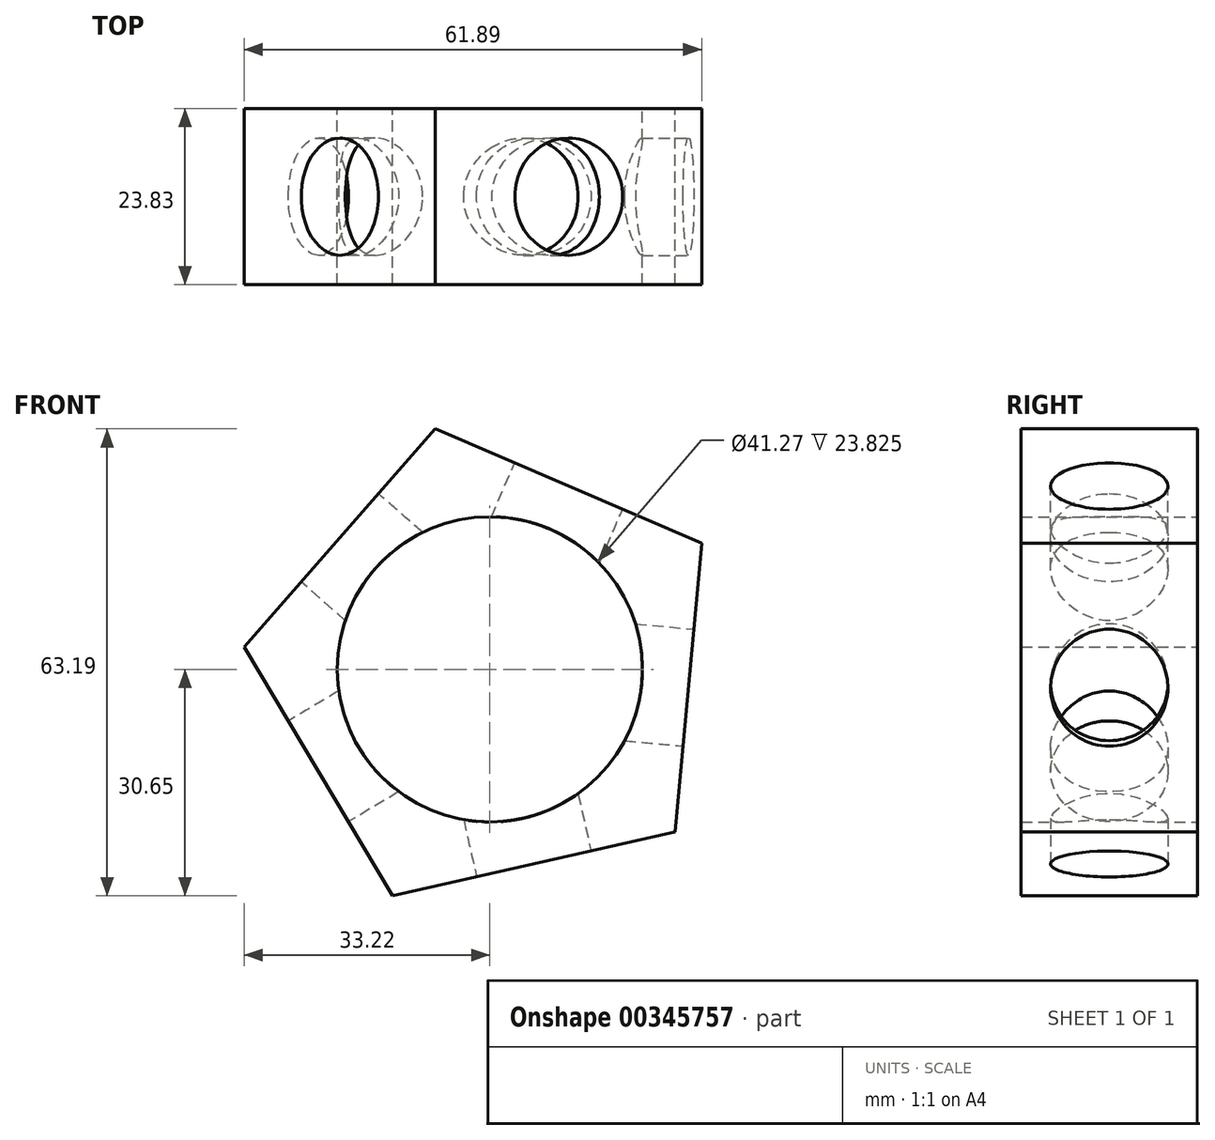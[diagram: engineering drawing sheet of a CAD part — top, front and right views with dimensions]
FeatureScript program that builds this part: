
annotation { "Feature Type Name" : "Feature", "Feature Type Description" : "" }
export const myFeature = defineFeature(function(context is Context, id is Id, definition is map)
    precondition{}
    {
        {
            var Q0;
            Q0=qCreatedBy(makeId("Front.planeOp"),FACE);
            var sketch = newSketch(context, id + "F0", { "sketchPlane" : qUnion([Q0])});
            skCircle(sketch, "E0.cCircle", {"center": v(0, 0) * mm, "radius": 26.99 * mm, "construction": true});
            skLineSegment(sketch, "E0.0", {"start": v(-33.22, 3.06) * mm, "end": v(-7.36, 32.54) * mm});
            skLineSegment(sketch, "E0.1", {"start": v(-7.36, 32.54) * mm, "end": v(28.67, 17.05) * mm});
            skLineSegment(sketch, "E0.2", {"start": v(28.67, 17.05) * mm, "end": v(25.08, -22) * mm});
            skLineSegment(sketch, "E0.3", {"start": v(25.08, -22) * mm, "end": v(-13.17, -30.65) * mm});
            skLineSegment(sketch, "E0.4", {"start": v(-13.17, -30.65) * mm, "end": v(-33.22, 3.06) * mm});
            skPoint(sketch, "E0.0.midPoint", {"position": v(-20.29, 17.8) * mm});
            skCircle(sketch, "E1", {"center": v(0, 0) * mm, "radius": 20.64 * mm});
            skSolve(sketch);
        }
        {
            var Q0;
            Q0=makeQuery(id+"F0.imprint","IMPRINT",FACE,{"disambiguationData":[TD([[makeQuery(id+"F0.imprint","IMPRINT",EDGE,{"derivedFrom":sQuery(id+"F0.wireOp",EDGE,"E0.0")}),-1.0]])]});
            extrude(context, id + "F1", {"entities" : qUnion([Q0]), "depth" : 23.83 * mm});
        }
        {
            var Q0;
            Q0=makeQuery(id+"F1.opExtrude","SWEPT_FACE",FACE,{"disambiguationData":[OSD([sQuery(id+"F0.wireOp",EDGE,"E0.2")])]});
            var sketch = newSketch(context, id + "F2", { "sketchPlane" : qUnion([Q0])});
            skPoint(sketch, "E2", {"position": v(-11.91, 0) * mm});
            skSolve(sketch);
        }
        {
            var Q0;
            Q0=sQuery(id+"F2.wireOp",VERTEX,"E2");
            var Q1;
            Q1=makeQuery(id+"F1.opExtrude","SWEPT_BODY",BODY,{"disambiguationData":[OSD([sQuery(id+"F0.wireOp",EDGE,"E0.0"),sQuery(id+"F0.wireOp",EDGE,"E0.1"),sQuery(id+"F0.wireOp",EDGE,"E0.2"),sQuery(id+"F0.wireOp",EDGE,"E0.3"),sQuery(id+"F0.wireOp",EDGE,"E0.4"),sQuery(id+"F0.wireOp",EDGE,"E1")])]});
            hole(context, id + "F3", {"style" : HoleStyle.SIMPLE, "endStyle" : HoleEndStyle.BLIND, "holeDiameter" : 15.88 * mm, "holeDepth" : 12.7 * mm, "isTappedThrough" : true, "tappedDepth" : 12.7 * mm, "tapClearance" : 3, "locations" : qUnion([Q0]), "scope" : qUnion([Q1])});
        }
        {
            var Q0;
            Q0=makeQuery(id+"F1.opExtrude","SWEPT_FACE",FACE,{"disambiguationData":[OSD([sQuery(id+"F0.wireOp",EDGE,"E0.1")])]});
            var sketch = newSketch(context, id + "F4", { "sketchPlane" : qUnion([Q0])});
            skPoint(sketch, "E3", {"position": v(0, -11.91) * mm});
            skSolve(sketch);
        }
        {
            var Q0;
            Q0=sQuery(id+"F4.wireOp",VERTEX,"E3");
            var Q1;
            Q1=makeQuery(id+"F1.opExtrude","SWEPT_BODY",BODY,{"disambiguationData":[OSD([sQuery(id+"F0.wireOp",EDGE,"E0.0"),sQuery(id+"F0.wireOp",EDGE,"E0.1"),sQuery(id+"F0.wireOp",EDGE,"E0.2"),sQuery(id+"F0.wireOp",EDGE,"E0.3"),sQuery(id+"F0.wireOp",EDGE,"E0.4"),sQuery(id+"F0.wireOp",EDGE,"E1")])]});
            hole(context, id + "F5", {"style" : HoleStyle.SIMPLE, "endStyle" : HoleEndStyle.BLIND, "holeDiameter" : 15.88 * mm, "holeDepth" : 12.7 * mm, "isTappedThrough" : true, "tappedDepth" : 12.7 * mm, "tapClearance" : 3, "locations" : qUnion([Q0]), "scope" : qUnion([Q1])});
        }
        {
            var Q0;
            Q0=makeQuery(id+"F1.opExtrude","SWEPT_FACE",FACE,{"disambiguationData":[OSD([sQuery(id+"F0.wireOp",EDGE,"E0.0")])]});
            var sketch = newSketch(context, id + "F6", { "sketchPlane" : qUnion([Q0])});
            skPoint(sketch, "E4", {"position": v(11.91, 0) * mm});
            skSolve(sketch);
        }
        {
            var Q0;
            Q0=sQuery(id+"F6.wireOp",VERTEX,"E4");
            var Q1;
            Q1=makeQuery(id+"F1.opExtrude","SWEPT_BODY",BODY,{"disambiguationData":[OSD([sQuery(id+"F0.wireOp",EDGE,"E0.0"),sQuery(id+"F0.wireOp",EDGE,"E0.1"),sQuery(id+"F0.wireOp",EDGE,"E0.2"),sQuery(id+"F0.wireOp",EDGE,"E0.3"),sQuery(id+"F0.wireOp",EDGE,"E0.4"),sQuery(id+"F0.wireOp",EDGE,"E1")])]});
            hole(context, id + "F7", {"style" : HoleStyle.SIMPLE, "endStyle" : HoleEndStyle.BLIND, "holeDiameter" : 15.88 * mm, "holeDepth" : 12.7 * mm, "isTappedThrough" : true, "tappedDepth" : 12.7 * mm, "tapClearance" : 3, "locations" : qUnion([Q0]), "scope" : qUnion([Q1])});
        }
        {
            var Q0;
            Q0=makeQuery(id+"F1.opExtrude","SWEPT_FACE",FACE,{"disambiguationData":[OSD([sQuery(id+"F0.wireOp",EDGE,"E0.4")])]});
            var sketch = newSketch(context, id + "F8", { "sketchPlane" : qUnion([Q0])});
            skPoint(sketch, "E5", {"position": v(11.91, 0) * mm});
            skSolve(sketch);
        }
        {
            var Q0;
            Q0=sQuery(id+"F8.wireOp",VERTEX,"E5");
            var Q1;
            Q1=makeQuery(id+"F1.opExtrude","SWEPT_BODY",BODY,{"disambiguationData":[OSD([sQuery(id+"F0.wireOp",EDGE,"E0.0"),sQuery(id+"F0.wireOp",EDGE,"E0.1"),sQuery(id+"F0.wireOp",EDGE,"E0.2"),sQuery(id+"F0.wireOp",EDGE,"E0.3"),sQuery(id+"F0.wireOp",EDGE,"E0.4"),sQuery(id+"F0.wireOp",EDGE,"E1")])]});
            hole(context, id + "F9", {"style" : HoleStyle.SIMPLE, "endStyle" : HoleEndStyle.BLIND, "holeDiameter" : 15.88 * mm, "holeDepth" : 12.7 * mm, "isTappedThrough" : true, "tappedDepth" : 12.7 * mm, "tapClearance" : 3, "locations" : qUnion([Q0]), "scope" : qUnion([Q1])});
        }
        {
            var Q0;
            Q0=makeQuery(id+"F1.opExtrude","SWEPT_FACE",FACE,{"disambiguationData":[OSD([sQuery(id+"F0.wireOp",EDGE,"E0.3")])]});
            var sketch = newSketch(context, id + "F10", { "sketchPlane" : qUnion([Q0])});
            skPoint(sketch, "E6", {"position": v(0, 11.91) * mm});
            skSolve(sketch);
        }
        {
            var Q0;
            Q0=sQuery(id+"F10.wireOp",VERTEX,"E6");
            var Q1;
            Q1=makeQuery(id+"F1.opExtrude","SWEPT_BODY",BODY,{"disambiguationData":[OSD([sQuery(id+"F0.wireOp",EDGE,"E0.0"),sQuery(id+"F0.wireOp",EDGE,"E0.1"),sQuery(id+"F0.wireOp",EDGE,"E0.2"),sQuery(id+"F0.wireOp",EDGE,"E0.3"),sQuery(id+"F0.wireOp",EDGE,"E0.4"),sQuery(id+"F0.wireOp",EDGE,"E1")])]});
            hole(context, id + "F11", {"style" : HoleStyle.SIMPLE, "endStyle" : HoleEndStyle.BLIND, "holeDiameter" : 15.88 * mm, "holeDepth" : 12.7 * mm, "isTappedThrough" : true, "tappedDepth" : 12.7 * mm, "tapClearance" : 3, "locations" : qUnion([Q0]), "scope" : qUnion([Q1])});
        }
    });
